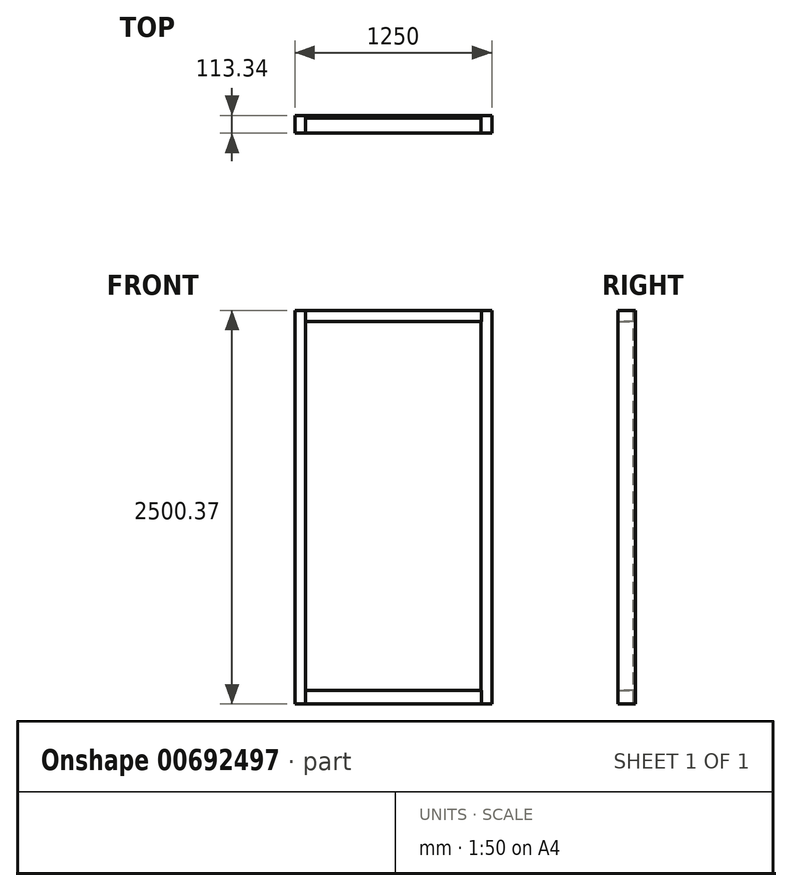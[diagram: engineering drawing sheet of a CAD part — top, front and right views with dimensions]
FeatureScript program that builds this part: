
annotation { "Feature Type Name" : "Feature", "Feature Type Description" : "" }
export const myFeature = defineFeature(function(context is Context, id is Id, definition is map)
    precondition{}
    {
        {
            var Q0;
            Q0=qCreatedBy(makeId("Front.planeOp"),FACE);
            var sketch = newSketch(context, id + "F0", { "sketchPlane" : qUnion([Q0])});
            skLineSegment(sketch, "E0.bottom", {"start": v(-621.4, 1489.45) * mm, "end": v(628.6, 1489.45) * mm});
            skLineSegment(sketch, "E0.top", {"start": v(-621.4, -1010.55) * mm, "end": v(628.6, -1010.55) * mm});
            skLineSegment(sketch, "E0.left", {"start": v(-621.4, 1489.45) * mm, "end": v(-621.4, -1010.55) * mm});
            skLineSegment(sketch, "E0.right", {"start": v(628.6, 1489.45) * mm, "end": v(628.6, -1010.55) * mm});
            skPoint(sketch, "E1", {"position": v(-553.4, 1489.45) * mm});
            skPoint(sketch, "E2", {"position": v(560.59, 1489.45) * mm});
            skLineSegment(sketch, "E3", {"start": v(-553.4, 1489.45) * mm, "end": v(-553.4, -1010.55) * mm});
            skLineSegment(sketch, "E4", {"start": v(560.59, 1489.45) * mm, "end": v(560.59, -1010.55) * mm});
            skSolve(sketch);
        }
        {
            var Q0;
            {var subQ0=sQuery(id+"F0.wireOp",EDGE,"E0.left");Q0=makeQuery(id+"F0.imprint","IMPRINT",FACE,{"disambiguationData":[TD([[makeQuery(id+"F0.imprint","IMPRINT",EDGE,{"derivedFrom":subQ0}),1.0]])]});}
            var Q1;
            {var subQ0=sQuery(id+"F0.wireOp",EDGE,"E0.right");Q1=makeQuery(id+"F0.imprint","IMPRINT",FACE,{"disambiguationData":[TD([[makeQuery(id+"F0.imprint","IMPRINT",EDGE,{"derivedFrom":subQ0}),-1.0]])]});}
            extrude(context, id + "F1", {"entities" : qUnion([Q0, Q1]), "depth" : 113 * mm, "offsetDistance" : 25.4 * mm});
        }
        {
            var Q0;
            {var subQ0=sQuery(id+"F0.wireOp",EDGE,"E3");Q0=makeQuery(id+"F0.imprint","IMPRINT",FACE,{"disambiguationData":[TD([[makeQuery(id+"F0.imprint","IMPRINT",EDGE,{"derivedFrom":subQ0}),1.0]])]});}
            extrude(context, id + "F2", {"entities" : qUnion([Q0]), "depth" : 18 * mm, "offsetDistance" : 25.4 * mm});
        }
        {
            var Q0;
            Q0=qCreatedBy(makeId("Top.planeOp"),FACE);
            var sketch = newSketch(context, id + "F3", { "sketchPlane" : qUnion([Q0])});
            skLineSegment(sketch, "E5", {"start": v(-554.22, 0) * mm, "end": v(-554.22, -113.34) * mm});
            skLineSegment(sketch, "E6", {"start": v(-554.22, -113.34) * mm, "end": v(561.4, -113.34) * mm});
            skLineSegment(sketch, "E7", {"start": v(561.4, -113.34) * mm, "end": v(561.4, 0) * mm});
            skLineSegment(sketch, "E8", {"start": v(-554.22, 0) * mm, "end": v(561.4, 0) * mm});
            skSolve(sketch);
        }
        {
            var Q0;
            Q0 = qSketchRegion(id + "F3", true);
            extrude(context, id + "F4", {"entities" : qUnion([Q0]), "depth" : 1488.44 * mm, "offsetDistance" : 25.4 * mm, "hasSecondDirection" : true, "secondDirectionOppositeDirection" : false, "secondDirectionDepth" : 1419.86 * mm});
        }
        {
            var Q0;
            Q0=makeQuery(id+"F3.imprint","IMPRINT",FACE,{"disambiguationData":[TD([[makeQuery(id+"F3.imprint","IMPRINT",EDGE,{"derivedFrom":sQuery(id+"F3.wireOp",EDGE,"E5")}),1.0]])]});
            extrude(context, id + "F5", {"entities" : qUnion([Q0]), "oppositeDirection" : true, "depth" : 1010.92 * mm, "offsetDistance" : 25.4 * mm, "hasSecondDirection" : true, "secondDirectionOppositeDirection" : true, "secondDirectionDepth" : 924.56 * mm});
        }
    });
